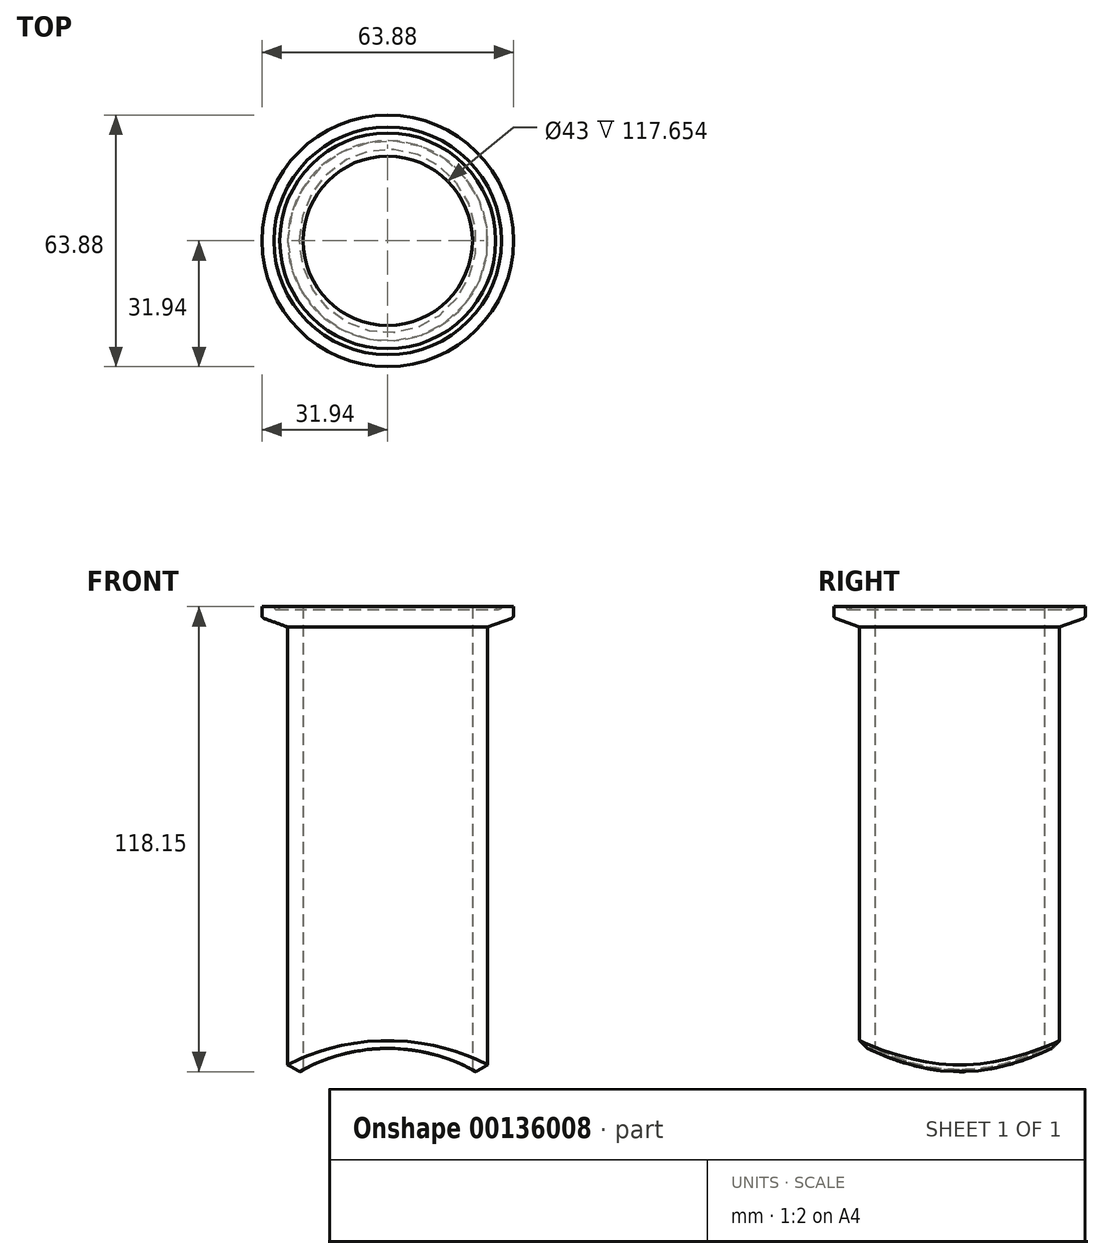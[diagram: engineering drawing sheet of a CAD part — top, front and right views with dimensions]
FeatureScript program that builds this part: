
annotation { "Feature Type Name" : "Feature", "Feature Type Description" : "" }
export const myFeature = defineFeature(function(context is Context, id is Id, definition is map)
    precondition{}
    {
        {
            var Q0;
            Q0=qCreatedBy(makeId("Right.planeOp"),FACE);
            var sketch = newSketch(context, id + "F0", { "sketchPlane" : qUnion([Q0])});
            skLineSegment(sketch, "E0", {"start": v(0, 0) * mm, "end": v(0, 123.67) * mm, "construction": true});
            skLineSegment(sketch, "E1", {"start": v(-25.4, 0) * mm, "end": v(-25.4, 114.82) * mm});
            skLineSegment(sketch, "E2", {"start": v(-25.4, 114.82) * mm, "end": v(-31.41, 117) * mm});
            skLineSegment(sketch, "E3", {"start": v(-31.94, 117.76) * mm, "end": v(-31.94, 120) * mm});
            skLineSegment(sketch, "E4", {"start": v(-31.94, 120) * mm, "end": v(-28.92, 120) * mm});
            skLineSegment(sketch, "E5", {"start": v(-21.5, 120) * mm, "end": v(-21.5, 0) * mm});
            skLineSegment(sketch, "E6", {"start": v(-25.4, 0) * mm, "end": v(-21.5, 0) * mm});
            skPoint(sketch, "E7.visualSharp", {"position": v(-31.94, 117.2) * mm});
            skArc(sketch, "E7.filletArc", {"start": v(-31.94, 117.76) * mm, "mid": v(-31.8, 117.3) * mm, "end": v(-31.41, 117) * mm});
            skArc(sketch, "E8", {"start": v(-28.92, 120) * mm, "mid": v(-28.17, 119.25) * mm, "end": v(-27.42, 120) * mm});
            skLineSegment(sketch, "E9.trimOffspring", {"start": v(-27.42, 120) * mm, "end": v(-21.5, 120) * mm});
            skSolve(sketch);
        }
        {
            var Q0;
            Q0 = qSketchRegion(id + "F0", true);
            var Q1;
            Q1=sQuery(id+"F0.wireOp",EDGE,"E0");
            revolve(context, id + "F1", {"entities" : qUnion([Q0]), "axis" : qUnion([Q1]), "revolveType" : RevolveType.FULL});
        }
        {
            var Q0;
            Q0=qCreatedBy(makeId("Front.planeOp"),FACE);
            var sketch = newSketch(context, id + "F2", { "sketchPlane" : qUnion([Q0])});
            skCircle(sketch, "E10", {"center": v(0, -37.75) * mm, "radius": 45.5 * mm});
            skLineSegment(sketch, "E11", {"start": v(0, 0) * mm, "end": v(25.4, 0) * mm, "construction": true});
            skSolve(sketch);
        }
        {
            var Q0;
            Q0 = qSketchRegion(id + "F2", true);
            extrude(context, id + "F3", {"entities" : qUnion([Q0]), "operationType" : NewBodyOperationType.REMOVE, "endBound" : BoundingType.SYMMETRIC, "oppositeDirection" : true, "depth" : 100 * mm});
        }
        {
            var Q0;
            Q0=makeQuery(id+"F3.boolean.opBoolean","INTERSECT",EDGE,{"derivedFrom":[makeQuery(id+"F1.opRevolve","SWEPT_FACE",FACE,{"disambiguationData":[OSD([sQuery(id+"F0.wireOp",EDGE,"E1")])]}),makeQuery(id+"F3.opExtrude","SWEPT_FACE",FACE,{"disambiguationData":[OSD([sQuery(id+"F2.wireOp",EDGE,"E10")])]})]});
            chamfer(context, id + "F4", {"entities" : qUnion([Q0]), "width" : 2 * mm, "tangentPropagation" : true});
        }
    });
